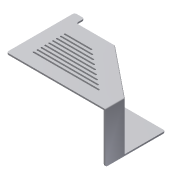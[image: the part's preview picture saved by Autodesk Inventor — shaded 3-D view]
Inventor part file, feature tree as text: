
AUTODESK INVENTOR PART (.ipt)
format: ipt  version: 2014 (Build 180170000, 170)  size: 205,312 bytes
history: native  units: mm
features: extrude x4, sketch x4, fillet x2
ambient origin geometry x8: Origin, YZ Plane, XZ Plane, XY Plane, X Axis, Y Axis, Z Axis, Center Point
bodies: Solid1 (feature_tree)
feature tree (10):
  extrude  "Extrusion1"  Depth=254.0mm
  extrude  "Extrusion2"  Depth=50.0mm
  extrude  "Extrusion3"  Depth=4.0mm
  fillet  "Fillet1"  Radius=4.0mm
  fillet  "Fillet2"  Radius=4.0mm
  extrude  "Extrusion4"  Depth=4.0mm
  sketch  "Sketch1"  dims[d0=175.0mm d1=254.0mm]
  sketch  "Sketch2"  dims[d2=25.0mm d3=50.0mm]
  sketch  "Sketch3"  dims[d4=21.0mm d5=100.0mm d6=4.0mm d7=0.0mm d8=4.0mm]
  sketch  "Sketch4"  dims[d9=4.0mm d10=4.0mm d11=125.0mm d12=0.0mm d13=4.0mm d14=0.0mm d15=5.0mm d16=2.0mm d17=2.0mm d18=6.0mm d19=6.0mm d20=6.0mm d21=6.0mm d22=6.0mm d23=6.0mm d24=35.0mm d25=35.0mm d26=50.0mm d27=6.0mm d28=6.0mm d29=4.0mm d30=0.0mm]
